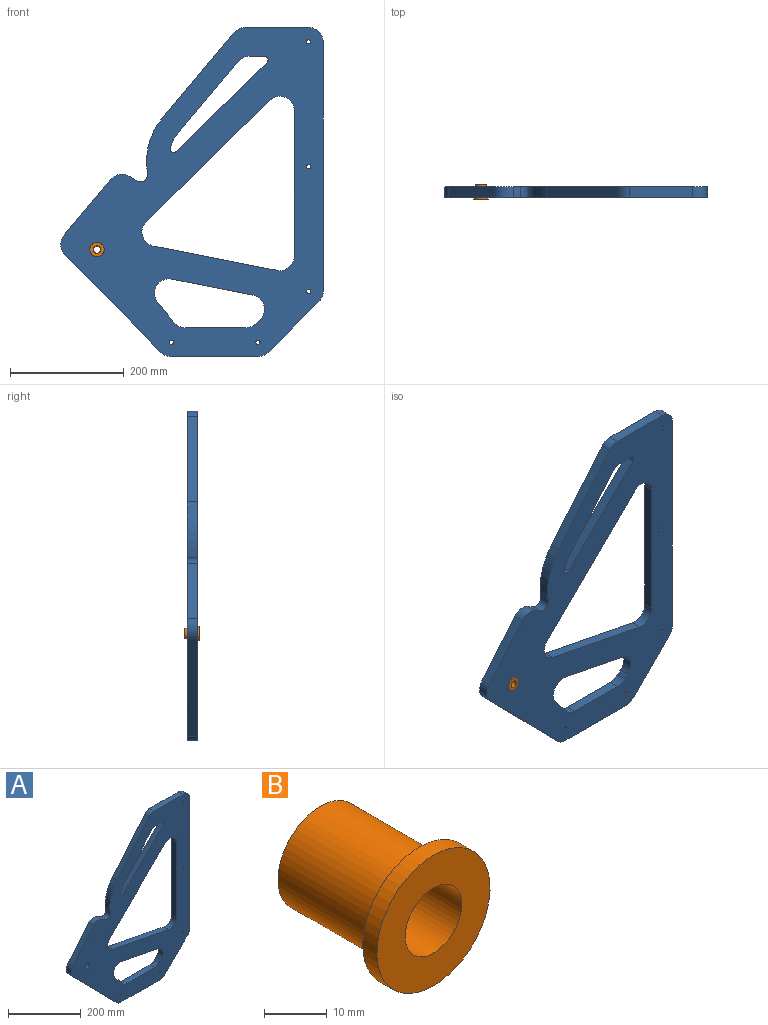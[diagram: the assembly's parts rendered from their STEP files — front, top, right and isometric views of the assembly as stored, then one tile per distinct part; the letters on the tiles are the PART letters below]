
ASSEMBLY  parts=2 mates=1
PART A: 46 faces, bbox 461.1x18.3x578.6 mm
  f0: cylinder r=6.35mm len=18.29mm, axis (0,1,0), area 307.8mm2, adj f2,f6,f7,f8
  f1: cylinder r=6.35mm len=18.29mm, axis (0,-1,0), area 274.7mm2, adj f2,f4,f7,f8
  f2: plane 159.43x156.41mm, normal (-0.7,0,0.71), area 4084.6mm2, adj f0,f1,f7,f8
  f3: cylinder r=25.4mm len=19.46mm, axis (0,-1,0), area 405.4mm2, adj f4,f5,f7,f8
  f4: plane 26.97x18.29mm, normal (0,0,-1), area 493.2mm2, adj f1,f3,f7,f8
  f5: plane 123.33x103.49mm, normal (0.77,0,-0.64), area 2944.3mm2, adj f3,f6,f7,f8
  f6: cylinder r=82.77mm len=28.46mm, axis (0,1,0), area 597.2mm2, adj f0,f5,f7,f8
  f7: plane 578.61x461.09mm, normal (0,1,0), area 114785.9mm2, adj f0,f1,f2,f3,f4,f5,f6,f9
  f8: plane 578.61x461.09mm, normal (0,-1,0), area 114785.9mm2, adj f0,f1,f2,f3,f4,f5,f6,f9
  f9: cylinder r=25.4mm len=19.82mm, axis (0,1,0), area 415.7mm2, adj f7,f8,f13,f15
  f10: cylinder r=25.4mm len=42.88mm, axis (0,-1,0), area 1003.9mm2, adj f7,f8,f12,f16
  f11: cylinder r=25.4mm len=41.29mm, axis (0,1,0), area 1134.2mm2, adj f7,f8,f12,f13
  f12: plane 142.21x28.08mm, normal (-0.19,0,-0.98), area 2650.9mm2, adj f7,f8,f10,f11
  f13: plane 35.13x28.17mm, normal (0.78,0,0.63), area 823.6mm2, adj f7,f8,f9,f11
  f14: cylinder r=25.4mm len=18.29mm, axis (0,-1,0), area 364.8mm2, adj f7,f8,f15,f16
  f15: plane 106.98x18.29mm, normal (0,0,1), area 1956.4mm2, adj f7,f8,f9,f14
  f16: plane 18.29x7.06mm, normal (-0.71,0,0.71), area 182.5mm2, adj f7,f8,f10,f14
  f17: cylinder r=25.4mm len=32.16mm, axis (0,1,0), area 648.6mm2, adj f7,f8,f29,f30
  f18: cylinder r=25.4mm len=19.46mm, axis (0,-1,0), area 405.4mm2, adj f7,f8,f20,f33
  f19: cylinder r=25.4mm len=25.4mm, axis (0,1,0), area 729.7mm2, adj f7,f8,f20,f22
  f20: plane 111.78x18.29mm, normal (0,0,1), area 2044.2mm2, adj f7,f8,f18,f19
  f21: cylinder r=25.4mm len=18.29mm, axis (0,1,0), area 364.8mm2, adj f7,f8,f22,f24
  f22: plane 438.56x18.29mm, normal (1,0,0), area 8020.3mm2, adj f7,f8,f19,f21
  f23: cylinder r=25.4mm len=18.29mm, axis (0,1,0), area 364.8mm2, adj f7,f8,f24,f26
  f24: plane 89.25x89.25mm, normal (0.71,0,-0.71), area 2308.4mm2, adj f7,f8,f21,f23
  f25: cylinder r=25.4mm len=18.29mm, axis (0,1,0), area 369.5mm2, adj f7,f8,f26,f28
  f26: plane 152.4x18.29mm, normal (0,0,-1), area 2787.1mm2, adj f7,f8,f23,f25
  f27: cylinder r=25.4mm len=34.11mm, axis (0,-1,0), area 684.5mm2, adj f7,f8,f28,f29
  f28: plane 172.06x168.64mm, normal (-0.71,0,-0.7), area 4406mm2, adj f7,f8,f25,f27
  f29: plane 97.46x81.78mm, normal (-0.77,0,0.64), area 2326.7mm2, adj f7,f8,f17,f27
  f30: plane 18.29x13.52mm, normal (0.5,0,0.87), area 285.6mm2, adj f7,f8,f17,f31
  f31: cylinder r=12.7mm len=19.05mm, axis (0,1,0), area 525mm2, adj f7,f8,f30,f32
  f32: cylinder r=120.87mm len=97.69mm, axis (0,1,0), area 1910.6mm2, adj f7,f8,f31,f33
  f33: plane 149.64x125.56mm, normal (-0.77,0,0.64), area 3572.4mm2, adj f7,f8,f18,f32
  f34: cylinder r=25.4mm len=30.32mm, axis (0,1,0), area 820.2mm2, adj f7,f8,f36,f39
  f35: cylinder r=25.4mm len=43.19mm, axis (0,-1,0), area 1090mm2, adj f7,f8,f36,f38
  f36: plane 255.75x18.29mm, normal (-1,0,0), area 4677.1mm2, adj f7,f8,f34,f35
  f37: cylinder r=25.4mm len=43.05mm, axis (0,1,0), area 1008.4mm2, adj f7,f8,f38,f39
  f38: plane 217.01x212.9mm, normal (0.7,0,-0.71), area 5559.7mm2, adj f7,f8,f35,f37
  f39: plane 217.01x42.85mm, normal (0.19,0,0.98), area 4045.3mm2, adj f7,f8,f34,f37
  f40: cylinder r=9.53mm len=19.05mm, axis (0,1,0), area 1094.5mm2, adj f7,f8
  f41: cylinder r=3.81mm len=18.29mm, axis (0,1,0), area 437.8mm2, adj f7,f8
  f42: cylinder r=3.81mm len=18.29mm, axis (0,1,0), area 437.8mm2, adj f7,f8
  f43: cylinder r=3.81mm len=18.29mm, axis (0,1,0), area 437.8mm2, adj f7,f8
  f44: cylinder r=3.81mm len=18.29mm, axis (0,1,0), area 437.8mm2, adj f7,f8
  f45: cylinder r=3.81mm len=18.29mm, axis (0,1,0), area 437.8mm2, adj f7,f8
PART B: 6 faces, bbox 25.4x25.4x25.4 mm
  f0: plane 19.05x19.05mm, normal (0,1,0), area 158.3mm2, adj f2,f4
  f1: cylinder r=12.7mm len=25.4mm, axis (0,1,0), area 253.4mm2, adj f3,f5
  f2: cylinder r=6.35mm len=25.4mm, axis (0,1,0), area 1013.4mm2, adj f0,f3
  f3: plane 25.4x25.4mm, normal (0,-1,0), area 380mm2, adj f1,f2
  f4: cylinder r=9.53mm len=22.23mm, axis (0,1,0), area 1330.1mm2, adj f0,f5
  f5: plane 25.4x25.4mm, normal (0,1,0), area 221.7mm2, adj f1,f4
PLACE A t=(-577.93,-1954.97,-66.91)mm
PLACE B t=(-654.13,-2473.26,-198.9)mm
MATE fastened B.f1 <-> A.f40  axis (0,1,0) through (-1000.87,-2495.49,197.41)mm
